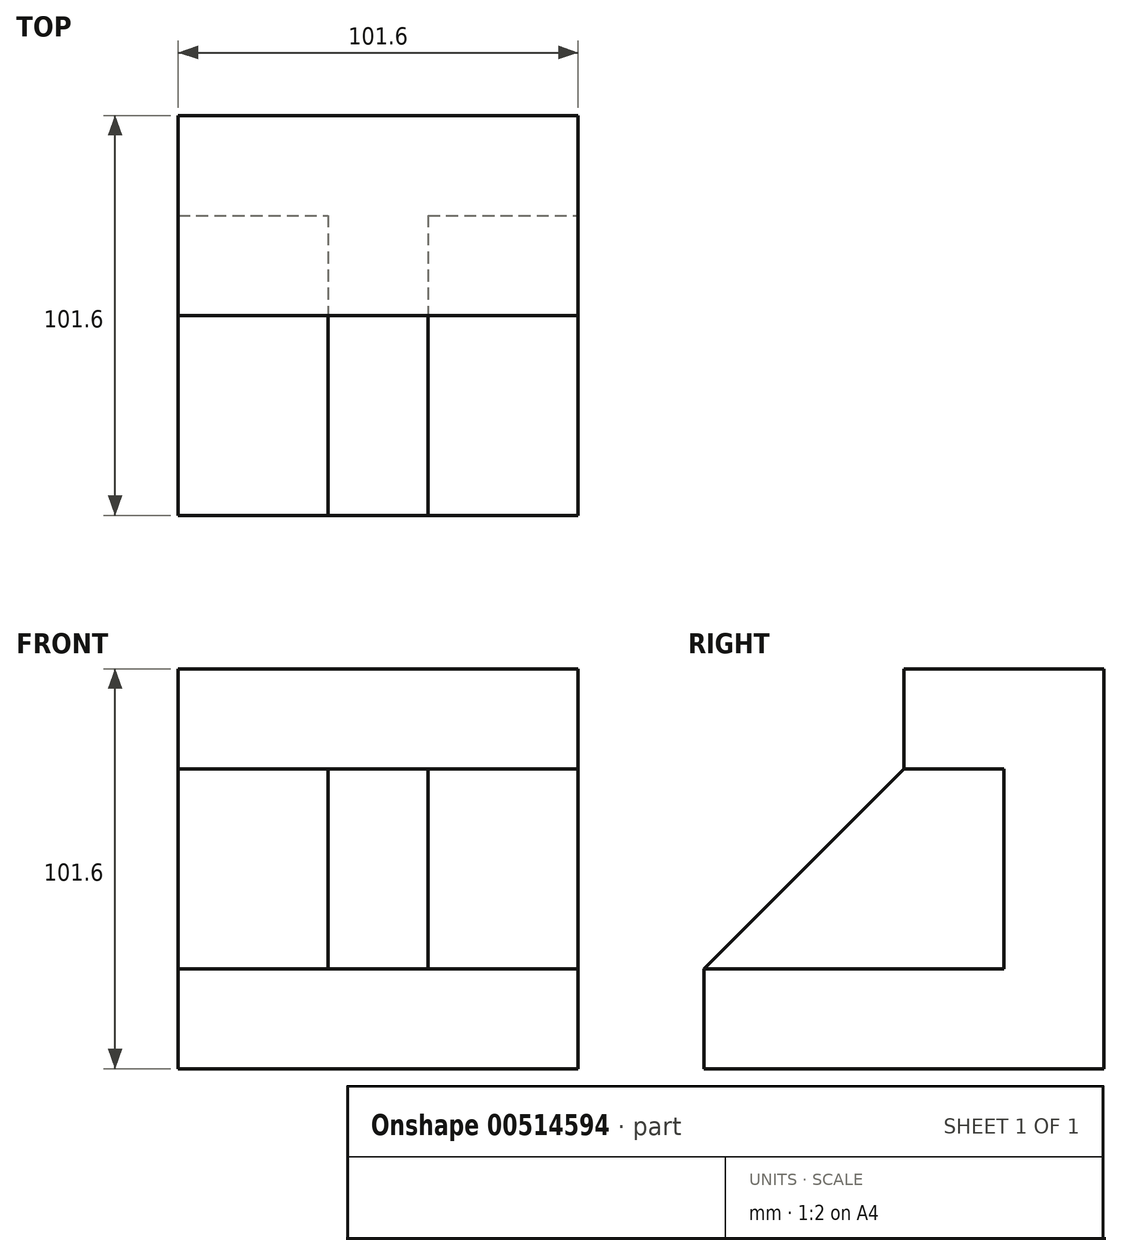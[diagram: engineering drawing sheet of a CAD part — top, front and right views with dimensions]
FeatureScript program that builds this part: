
annotation { "Feature Type Name" : "Feature", "Feature Type Description" : "" }
export const myFeature = defineFeature(function(context is Context, id is Id, definition is map)
    precondition{}
    {
        {
            var Q0;
            Q0=qCreatedBy(makeId("Front.planeOp"),FACE);
            var sketch = newSketch(context, id + "F0", { "sketchPlane" : qUnion([Q0])});
            skLineSegment(sketch, "E0.bottom", {"start": v(0, 0) * mm, "end": v(-101.6, 0) * mm});
            skLineSegment(sketch, "E0.top", {"start": v(0, -101.6) * mm, "end": v(-101.6, -101.6) * mm});
            skLineSegment(sketch, "E0.left", {"start": v(0, 0) * mm, "end": v(0, -101.6) * mm});
            skLineSegment(sketch, "E0.right", {"start": v(-101.6, 0) * mm, "end": v(-101.6, -101.6) * mm});
            skSolve(sketch);
        }
        {
            var Q0;
            Q0=makeQuery(id+"F0.imprint","IMPRINT",FACE,{"disambiguationData":[TD([[makeQuery(id+"F0.imprint","IMPRINT",EDGE,{"derivedFrom":sQuery(id+"F0.wireOp",EDGE,"E0.bottom")}),1.0]])]});
            extrude(context, id + "F1", {"entities" : qUnion([Q0]), "depth" : 101.6 * mm, "offsetDistance" : 25.4 * mm});
        }
        {
            var Q0;
            Q0=makeQuery(id+"F1.opExtrude","SWEPT_FACE",FACE,{"disambiguationData":[OSD([sQuery(id+"F0.wireOp",EDGE,"E0.left")])]});
            var sketch = newSketch(context, id + "F2", { "sketchPlane" : qUnion([Q0])});
            skLineSegment(sketch, "E1", {"start": v(0, 0) * mm, "end": v(-39.59, -5.82) * mm});
            skLineSegment(sketch, "E2", {"start": v(-37.86, -5.82) * mm, "end": v(-39.59, -5.82) * mm});
            skLineSegment(sketch, "E3", {"start": v(0, 0) * mm, "end": v(-50.8, 0) * mm});
            skLineSegment(sketch, "E4", {"start": v(0, 0) * mm, "end": v(0, -76.2) * mm});
            skLineSegment(sketch, "E5", {"start": v(0, -76.2) * mm, "end": v(-101.6, -76.2) * mm});
            skLineSegment(sketch, "E6", {"start": v(-50.8, 0) * mm, "end": v(-50.8, -25.4) * mm});
            skLineSegment(sketch, "E7", {"start": v(-50.8, -25.4) * mm, "end": v(-25.4, -25.4) * mm});
            skLineSegment(sketch, "E8", {"start": v(-25.4, -25.4) * mm, "end": v(-25.4, -76.2) * mm});
            skSolve(sketch);
        }
        {
            var Q0;
            {var subQ1=sQuery(id+"F2.wireOp",EDGE,"E6");Q0=makeQuery(id+"F2.imprint","IMPRINT",FACE,{"disambiguationData":[TD([[makeQuery(id+"F2.imprint","IMPRINT",EDGE,{"derivedFrom":subQ1}),-1.0]])]});}
            extrude(context, id + "F3", {"entities" : qUnion([Q0]), "operationType" : NewBodyOperationType.REMOVE, "oppositeDirection" : true, "depth" : 121.67 * mm, "offsetDistance" : 25.4 * mm});
        }
        {
            var Q0;
            Q0=makeQuery(id+"F3.boolean.opBoolean","COPY",FACE,{"derivedFrom":makeQuery(id+"F3.opExtrude","SWEPT_FACE",FACE,{"disambiguationData":[OSD([sQuery(id+"F2.wireOp",EDGE,"E5")])]})});
            var sketch = newSketch(context, id + "F4", { "sketchPlane" : qUnion([Q0])});
            skLineSegment(sketch, "E9", {"start": v(0, -25.4) * mm, "end": v(-38.1, -25.4) * mm});
            skLineSegment(sketch, "E10", {"start": v(-101.6, -25.4) * mm, "end": v(-63.5, -25.4) * mm});
            skLineSegment(sketch, "E11", {"start": v(-101.6, -101.6) * mm, "end": v(-63.5, -101.6) * mm});
            skLineSegment(sketch, "E12", {"start": v(0, -101.6) * mm, "end": v(-38.1, -101.6) * mm});
            skLineSegment(sketch, "E13", {"start": v(-63.5, -25.4) * mm, "end": v(-38.1, -25.4) * mm});
            skLineSegment(sketch, "E14", {"start": v(-38.1, -25.4) * mm, "end": v(-38.1, -101.6) * mm});
            skLineSegment(sketch, "E15", {"start": v(-63.5, -25.4) * mm, "end": v(-63.5, -101.6) * mm});
            skLineSegment(sketch, "E16", {"start": v(-63.5, -101.6) * mm, "end": v(-38.1, -101.6) * mm});
            skSolve(sketch);
        }
        {
            var Q0;
            Q0=makeQuery(id+"F4.imprint","IMPRINT",FACE,{"disambiguationData":[TD([[makeQuery(id+"F4.imprint","IMPRINT",EDGE,{"derivedFrom":sQuery(id+"F4.wireOp",EDGE,"E14")}),-1.0]])]});
            extrude(context, id + "F5", {"entities" : qUnion([Q0]), "operationType" : NewBodyOperationType.ADD, "depth" : 50.8 * mm, "offsetDistance" : 25.4 * mm});
        }
        {
            var Q0;
            Q0=makeQuery(id+"F5.opExtrude","SWEPT_FACE",FACE,{"disambiguationData":[OSD([sQuery(id+"F4.wireOp",EDGE,"E14")])]});
            var sketch = newSketch(context, id + "F6", { "sketchPlane" : qUnion([Q0])});
            skLineSegment(sketch, "E17", {"start": v(-25.4, -25.4) * mm, "end": v(-50.8, -25.4) * mm});
            skLineSegment(sketch, "E18", {"start": v(-50.8, -25.4) * mm, "end": v(-92.06, -25.4) * mm});
            skLineSegment(sketch, "E19", {"start": v(-50.8, -25.4) * mm, "end": v(-101.6, -76.2) * mm});
            skLineSegment(sketch, "E20", {"start": v(-101.6, -76.2) * mm, "end": v(-101.6, -25.4) * mm});
            skLineSegment(sketch, "E21", {"start": v(-101.6, -25.4) * mm, "end": v(-50.8, -25.4) * mm});
            skSolve(sketch);
        }
        {
            var Q0;
            {var subQ0=sQuery(id+"F6.wireOp",EDGE,"E19");Q0=makeQuery(id+"F6.imprint","IMPRINT",FACE,{"disambiguationData":[TD([[makeQuery(id+"F6.imprint","IMPRINT",EDGE,{"derivedFrom":subQ0}),-1.0]])]});}
            extrude(context, id + "F7", {"entities" : qUnion([Q0]), "operationType" : NewBodyOperationType.REMOVE, "oppositeDirection" : true, "depth" : 99.57 * mm, "offsetDistance" : 25.4 * mm});
        }
    });
